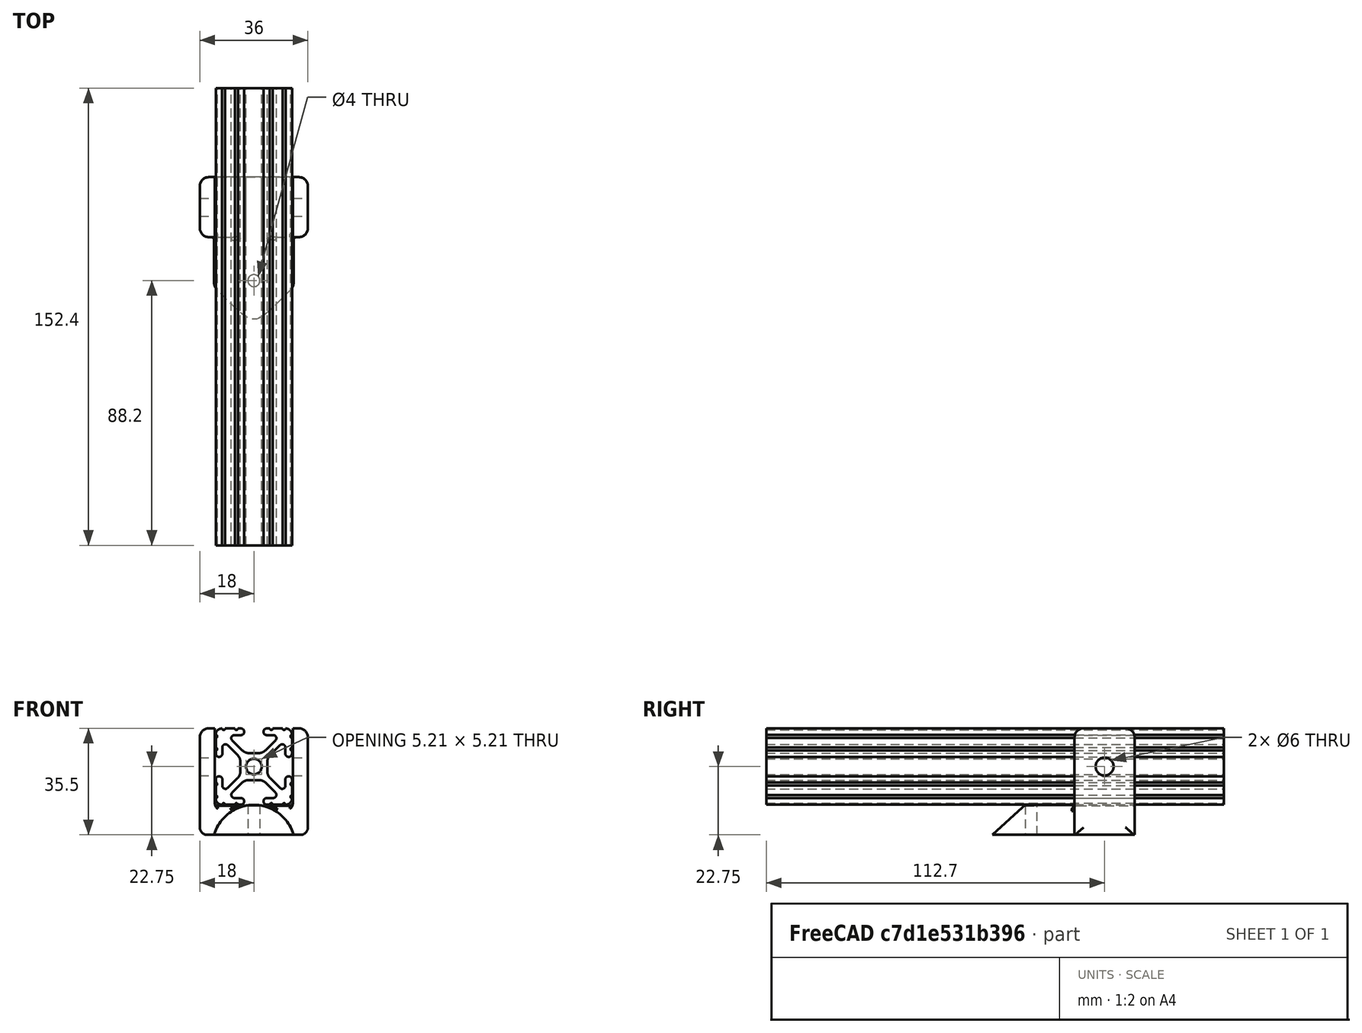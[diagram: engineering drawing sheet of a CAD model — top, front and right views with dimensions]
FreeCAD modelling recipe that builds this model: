
FCSTD DOCUMENT  (FreeCAD 0.20R29410 (Git))
Label: airModuleHolder11_21_2022
License: All rights reserved
LicenseURL: http://en.wikipedia.org/wiki/All_rights_reserved
objects: Part::Cut×6, Part::Cylinder×5, Part::Box×5, Part::Fillet×5, Part::MultiFuse×3, Part::Cone×1, Part::Feature×1
note: 26 computed .brp shape members not serialized (recipe doc carries the construction recipe); baked Part::Feature solids carry a one-line shape summary decoded from their .brp

FEATURE [Part::Cylinder] Cylinder
  Angle = 360
  AttacherType = Attacher::AttachEngine3D
  FirstAngle = 0
  Height = 36.5
  Placement = pos=(13.5,47.5,43) rot=(0,0.707107,-0.707107;3.14159rad)
  Radius = 13.75
  SecondAngle = 0
FEATURE [Part::Box] Box015  label="TSlotMount001"
  AttacherType = Attacher::AttachEngine3D
  Height = 35.5
  Length = 36
  Placement = pos=(-4.5,27.5,46.75) rot=(0,0,1;0rad)
  Width = 20
FEATURE [Part::Cylinder] Cylinder009  label="m5Cut"
  Angle = 360
  AttacherType = Attacher::AttachEngine3D
  FirstAngle = 0
  Height = 100
  Placement = pos=(-57.4,37.5,69.5) rot=(0,1,0;1.5708rad)
  Radius = 3
  SecondAngle = 0
FEATURE [Part::Box] Box016  label="Shell_Holder002"
  AttacherType = Attacher::AttachEngine3D
  Height = 20
  Length = 29
  Placement = pos=(-1,-20.5,26.75) rot=(0,0,1;0rad)
  Width = 75
FEATURE [Part::Box] Box018  label="TSlotFrameCut001"
  AttacherType = Attacher::AttachEngine3D
  Height = 28.5
  Length = 26
  Placement = pos=(0.5,0,56.5) rot=(0,0,1;0rad)
  Width = 254
FEATURE [Part::Cut] Cut009  label="TSlotMount002"
  Base = -> Box015
  Tool = -> Box018
FEATURE [Part::Cylinder] Cylinder015
  Angle = 360
  AttacherType = Attacher::AttachEngine3D
  FirstAngle = 0
  Height = 12
  Placement = pos=(13.5,13,45) rot=(0,0,1;1.5708rad)
  Radius = 2
  SecondAngle = 0
FEATURE [Part::Cone] Cone
  Angle = 180
  AttacherType = Attacher::AttachEngine3D
  Height = 15
  Placement = pos=(13.5,11,43) rot=(1,0,0;1.5708rad)
  Radius1 = 13.75
  Radius2 = 0
FEATURE [Part::MultiFuse] Fusion  label="beak"
  Shapes = -> [Cylinder,Cone]
FEATURE [Part::Cut] Cut
  Base = -> Fusion
  Tool = -> Box016
FEATURE [Part::Cut] Cut010
  Base = -> Cut009
  Tool = -> Cylinder009
FEATURE [Part::MultiFuse] Fusion002
  Shapes = -> [Cut,Cut010]
FEATURE [Part::Feature] Part__Feature  label="47065T801_T-Slotted Framing"
  Placement = pos=(13.5,1,69.5) rot=(1,0,0;1.5708rad)
  shape: bbox 25.4 x 152.4 x 25.4 mm, 108 faces (baked)
FEATURE [Part::Cylinder] Cylinder016
  Angle = 90
  AttacherType = Attacher::AttachEngine3D
  FirstAngle = 0
  Height = 50
  Placement = pos=(-2,50,49.25) rot=(0,-0.707107,0.707107;3.14159rad)
  Radius = 2.5
  SecondAngle = 0
FEATURE [Part::Box] Box019  label="Cube"
  AttacherType = Attacher::AttachEngine3D
  Height = 2.5
  Length = 2.5
  Placement = pos=(-4.5,0,46.75) rot=(0,0,1;0rad)
  Width = 50
FEATURE [Part::Cut] Cut012
  Base = -> Box019
  Tool = -> Cylinder016
FEATURE [Part::Box] Box020  label="Cube001"
  AttacherType = Attacher::AttachEngine3D
  Height = 2.5
  Length = 2.5
  Placement = pos=(-4.5,0,46.75) rot=(0,0,1;0rad)
  Width = 50
FEATURE [Part::Cylinder] Cylinder017
  Angle = 90
  AttacherType = Attacher::AttachEngine3D
  FirstAngle = 0
  Height = 50
  Placement = pos=(-2,50,49.25) rot=(0,0.707107,-0.707107;3.14159rad)
  Radius = 2.5
  SecondAngle = 0
FEATURE [Part::Cut] Cut013
  Base = -> Box020
  Placement = pos=(78.25,0,51.25) rot=(0,1,0;4.71239rad)
  Tool = -> Cylinder017
FEATURE [Part::Fillet] Fillet
  Base = -> Fusion002
  Edges = 6 edges r=1: [Edge26,Edge28,Edge36,Edge38,Edge44,Edge46]
FEATURE [Part::Fillet] Fillet001
  Base = -> Fillet
  Edges = 2 edges r=3: [Edge4,Edge26]
FEATURE [Part::Fillet] Fillet002
  Base = -> Fillet001
  Edges = 2 edges r=3: [Edge48,Edge71]
FEATURE [Part::Fillet] Fillet003
  Base = -> Fillet002
  Edges = 1 edges r=3: [Edge57]
FEATURE [Part::Fillet] Fillet004
  Base = -> Fillet003
  Edges = 2 edges r=3: [Edge60,Edge73]
FEATURE [Part::MultiFuse] Fusion003  label="cuts"
  Shapes = -> [Cut013,Cut012,Cylinder015]
FEATURE [Part::Cut] Cut014
  Base = -> Fillet004
  Tool = -> Fusion003
